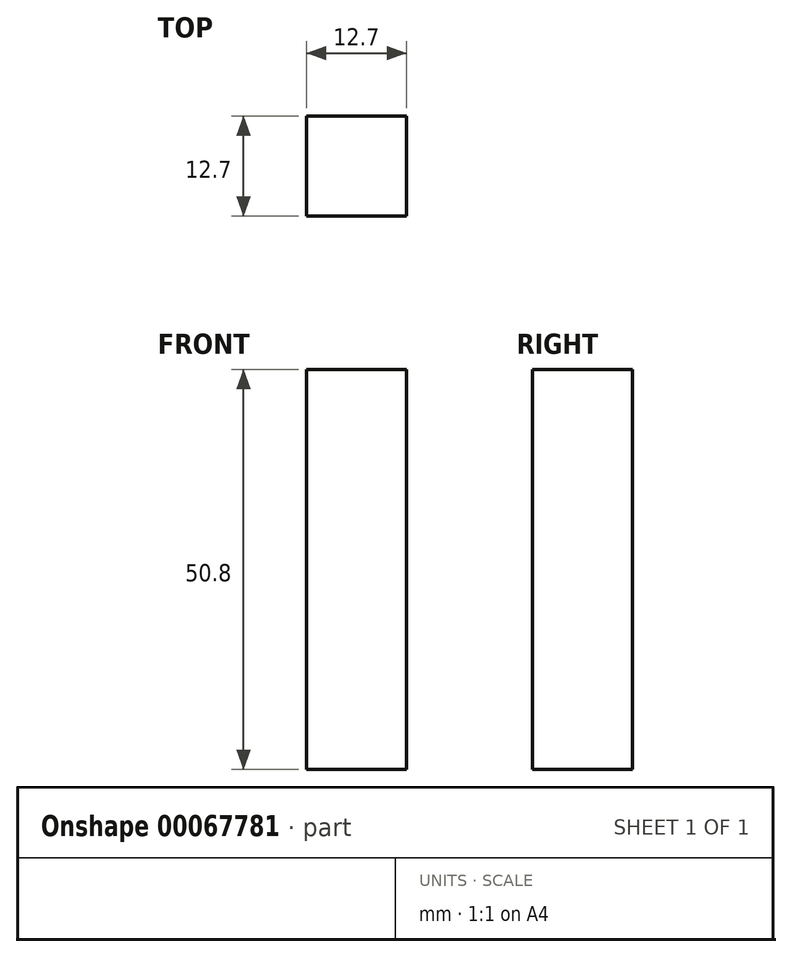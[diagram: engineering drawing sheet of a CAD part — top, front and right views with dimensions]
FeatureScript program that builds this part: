
annotation { "Feature Type Name" : "Feature", "Feature Type Description" : "" }
export const myFeature = defineFeature(function(context is Context, id is Id, definition is map)
    precondition{}
    {
        {
            var Q0;
            Q0=qCreatedBy(makeId("Front.planeOp"),FACE);
            var sketch = newSketch(context, id + "F0", { "sketchPlane" : qUnion([Q0])});
            skLineSegment(sketch, "E0", {"start": v(-7.26, 31.58) * mm, "end": v(5.44, 31.58) * mm});
            skLineSegment(sketch, "E1", {"start": v(5.44, 31.58) * mm, "end": v(5.44, -19.22) * mm});
            skLineSegment(sketch, "E2", {"start": v(5.44, -19.22) * mm, "end": v(-7.26, -19.22) * mm});
            skLineSegment(sketch, "E3", {"start": v(-7.26, -19.22) * mm, "end": v(-7.26, 31.58) * mm});
            skSolve(sketch);
        }
        {
            var Q0;
            Q0=makeQuery(id+"F0.imprint","IMPRINT",FACE,{"disambiguationData":[TD([[makeQuery(id+"F0.imprint","IMPRINT",EDGE,{"derivedFrom":sQuery(id+"F0.wireOp",EDGE,"E0")}),-1.0]])]});
            extrude(context, id + "F1", {"entities" : qUnion([Q0]), "depth" : 12.7 * mm});
        }
    });
